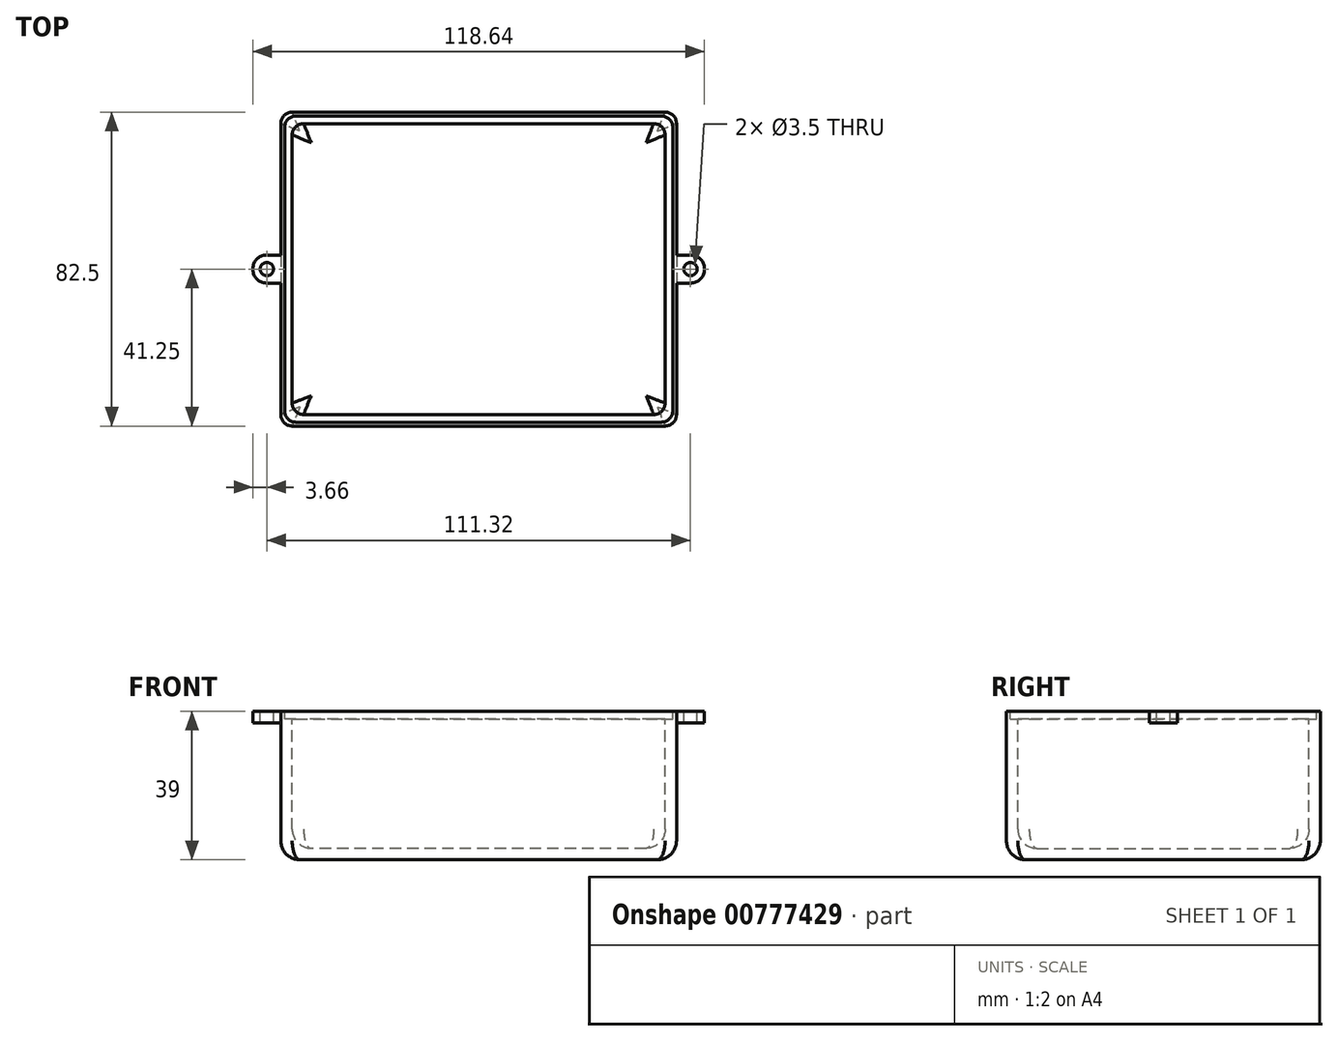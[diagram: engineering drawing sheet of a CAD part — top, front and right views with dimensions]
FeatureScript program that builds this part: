
annotation { "Feature Type Name" : "Feature", "Feature Type Description" : "" }
export const myFeature = defineFeature(function(context is Context, id is Id, definition is map)
    precondition{}
    {
        {
            var Q0;
            Q0=qCreatedBy(makeId("Top.planeOp"),FACE);
            var sketch = newSketch(context, id + "F0", { "sketchPlane" : qUnion([Q0])});
            skLineSegment(sketch, "E0.bottom", {"start": v(-52, 41.25) * mm, "end": v(52, 41.25) * mm});
            skLineSegment(sketch, "E0.top", {"start": v(-52, -41.25) * mm, "end": v(52, -41.25) * mm});
            skLineSegment(sketch, "E0.left", {"start": v(-52, 41.25) * mm, "end": v(-52, -41.25) * mm});
            skLineSegment(sketch, "E0.right", {"start": v(52, 41.25) * mm, "end": v(52, -41.25) * mm});
            skSolve(sketch);
        }
        {
            var Q0;
            Q0=makeQuery(id+"F0.imprint","IMPRINT",FACE,{"disambiguationData":[TD([[makeQuery(id+"F0.imprint","IMPRINT",EDGE,{"derivedFrom":sQuery(id+"F0.wireOp",EDGE,"E0.bottom")}),-1.0]])]});
            extrude(context, id + "F1", {"entities" : qUnion([Q0]), "depth" : 39 * mm, "offsetDistance" : 25 * mm});
        }
        {
            var Q0;
            Q0=makeQuery(id+"F1.opExtrude","CAP_FACE",FACE,{"disambiguationData":[OSD([sQuery(id+"F0.wireOp",EDGE,"E0.bottom"),sQuery(id+"F0.wireOp",EDGE,"E0.top"),sQuery(id+"F0.wireOp",EDGE,"E0.left"),sQuery(id+"F0.wireOp",EDGE,"E0.right")])],"isStart":false});
            var sketch = newSketch(context, id + "F2", { "sketchPlane" : qUnion([Q0])});
            skLineSegment(sketch, "E1.bottom", {"start": v(-49, 38.25) * mm, "end": v(49, 38.25) * mm});
            skLineSegment(sketch, "E1.top", {"start": v(-49, -38.25) * mm, "end": v(49, -38.25) * mm});
            skLineSegment(sketch, "E1.left", {"start": v(-49, 38.25) * mm, "end": v(-49, -38.25) * mm});
            skLineSegment(sketch, "E1.right", {"start": v(49, 38.25) * mm, "end": v(49, -38.25) * mm});
            skSolve(sketch);
        }
        {
            var Q0;
            Q0=makeQuery(id+"F2.imprint","IMPRINT",FACE,{"disambiguationData":[TD([[makeQuery(id+"F2.imprint","IMPRINT",EDGE,{"derivedFrom":sQuery(id+"F2.wireOp",EDGE,"E1.bottom")}),-1.0]])]});
            var Q1;
            Q1=makeQuery(id+"F1.opExtrude","CAP_FACE",FACE,{"disambiguationData":[OSD([sQuery(id+"F0.wireOp",EDGE,"E0.bottom"),sQuery(id+"F0.wireOp",EDGE,"E0.top"),sQuery(id+"F0.wireOp",EDGE,"E0.left"),sQuery(id+"F0.wireOp",EDGE,"E0.right")])],"isStart":true});
            extrude(context, id + "F3", {"entities" : qUnion([Q0]), "operationType" : NewBodyOperationType.REMOVE, "endBound" : BoundingType.UP_TO_SURFACE, "oppositeDirection" : true, "depth" : 25 * mm, "endBoundEntityFace" : qUnion([Q1]), "hasOffset" : true, "offsetDistance" : 3 * mm});
        }
        {
            var Q0;
            Q0=makeQuery(id+"F1.opExtrude","CAP_FACE",FACE,{"disambiguationData":[OSD([sQuery(id+"F0.wireOp",EDGE,"E0.bottom"),sQuery(id+"F0.wireOp",EDGE,"E0.top"),sQuery(id+"F0.wireOp",EDGE,"E0.left"),sQuery(id+"F0.wireOp",EDGE,"E0.right")])],"isStart":false});
            var sketch = newSketch(context, id + "F4", { "sketchPlane" : qUnion([Q0])});
            skLineSegment(sketch, "E2.bottom", {"start": v(-51, 40.25) * mm, "end": v(51, 40.25) * mm});
            skLineSegment(sketch, "E2.top", {"start": v(-51, -40.25) * mm, "end": v(51, -40.25) * mm});
            skLineSegment(sketch, "E2.left", {"start": v(-51, 40.25) * mm, "end": v(-51, -40.25) * mm});
            skLineSegment(sketch, "E2.right", {"start": v(51, 40.25) * mm, "end": v(51, -40.25) * mm});
            skSolve(sketch);
        }
        {
            var Q0;
            Q0 = qSketchRegion(id + "F4", true);
            extrude(context, id + "F5", {"entities" : qUnion([Q0]), "operationType" : NewBodyOperationType.REMOVE, "oppositeDirection" : true, "depth" : 2 * mm, "offsetDistance" : 25 * mm});
        }
        {
            var Q0;
            Q0=makeQuery(id+"F1.opExtrude","SWEPT_EDGE",EDGE,{"disambiguationData":[OSD([sQuery(id+"F0.wireOp",EDGE,"E0.top"),sQuery(id+"F0.wireOp",EDGE,"E0.left")])]});
            var Q1;
            Q1=makeQuery(id+"F1.opExtrude","SWEPT_EDGE",EDGE,{"disambiguationData":[OSD([sQuery(id+"F0.wireOp",EDGE,"E0.top"),sQuery(id+"F0.wireOp",EDGE,"E0.right")])]});
            var Q2;
            Q2=makeQuery(id+"F1.opExtrude","SWEPT_EDGE",EDGE,{"disambiguationData":[OSD([sQuery(id+"F0.wireOp",EDGE,"E0.bottom"),sQuery(id+"F0.wireOp",EDGE,"E0.right")])]});
            var Q3;
            Q3=makeQuery(id+"F1.opExtrude","SWEPT_EDGE",EDGE,{"disambiguationData":[OSD([sQuery(id+"F0.wireOp",EDGE,"E0.bottom"),sQuery(id+"F0.wireOp",EDGE,"E0.left")])]});
            var Q4;
            Q4=makeQuery(id+"F5.boolean.opBoolean","COPY",EDGE,{"derivedFrom":makeQuery(id+"F5.opExtrude","SWEPT_EDGE",EDGE,{"disambiguationData":[OSD([sQuery(id+"F4.wireOp",EDGE,"E2.top"),sQuery(id+"F4.wireOp",EDGE,"E2.left")])]})});
            var Q5;
            Q5=makeQuery(id+"F3.boolean.opBoolean","COPY",EDGE,{"derivedFrom":makeQuery(id+"F3.opExtrude","SWEPT_EDGE",EDGE,{"disambiguationData":[OSD([sQuery(id+"F2.wireOp",EDGE,"E1.top"),sQuery(id+"F2.wireOp",EDGE,"E1.left")])]})});
            var Q6;
            Q6=makeQuery(id+"F5.boolean.opBoolean","COPY",EDGE,{"derivedFrom":makeQuery(id+"F5.opExtrude","SWEPT_EDGE",EDGE,{"disambiguationData":[OSD([sQuery(id+"F4.wireOp",EDGE,"E2.bottom"),sQuery(id+"F4.wireOp",EDGE,"E2.left")])]})});
            var Q7;
            Q7=makeQuery(id+"F3.boolean.opBoolean","COPY",EDGE,{"derivedFrom":makeQuery(id+"F3.opExtrude","SWEPT_EDGE",EDGE,{"disambiguationData":[OSD([sQuery(id+"F2.wireOp",EDGE,"E1.bottom"),sQuery(id+"F2.wireOp",EDGE,"E1.left")])]})});
            var Q8;
            Q8=makeQuery(id+"F3.boolean.opBoolean","COPY",EDGE,{"derivedFrom":makeQuery(id+"F3.opExtrude","SWEPT_EDGE",EDGE,{"disambiguationData":[OSD([sQuery(id+"F2.wireOp",EDGE,"E1.bottom"),sQuery(id+"F2.wireOp",EDGE,"E1.right")])]})});
            var Q9;
            Q9=makeQuery(id+"F5.boolean.opBoolean","COPY",EDGE,{"derivedFrom":makeQuery(id+"F5.opExtrude","SWEPT_EDGE",EDGE,{"disambiguationData":[OSD([sQuery(id+"F4.wireOp",EDGE,"E2.bottom"),sQuery(id+"F4.wireOp",EDGE,"E2.right")])]})});
            var Q10;
            Q10=makeQuery(id+"F3.boolean.opBoolean","COPY",EDGE,{"derivedFrom":makeQuery(id+"F3.opExtrude","SWEPT_EDGE",EDGE,{"disambiguationData":[OSD([sQuery(id+"F2.wireOp",EDGE,"E1.top"),sQuery(id+"F2.wireOp",EDGE,"E1.right")])]})});
            var Q11;
            Q11=makeQuery(id+"F5.boolean.opBoolean","COPY",EDGE,{"derivedFrom":makeQuery(id+"F5.opExtrude","SWEPT_EDGE",EDGE,{"disambiguationData":[OSD([sQuery(id+"F4.wireOp",EDGE,"E2.top"),sQuery(id+"F4.wireOp",EDGE,"E2.right")])]})});
            fillet(context, id + "F6", {"entities" : qUnion([Q0, Q1, Q2, Q3, Q4, Q5, Q6, Q7, Q8, Q9, Q10, Q11]), "radius" : 3 * mm, "tangentPropagation" : true, "allowEdgeOverflow" : false});
        }
        {
            var Q0;
            Q0=makeQuery(id+"F1.opExtrude","CAP_EDGE",EDGE,{"disambiguationData":[OSD([sQuery(id+"F0.wireOp",EDGE,"E0.left")])],"isStart":true});
            var Q1;
            {var subQ0=sQuery(id+"F0.wireOp",EDGE,"E0.left");var subQ1=sQuery(id+"F0.wireOp",EDGE,"E0.top");Q1=makeQuery(id+"F6.opFillet","BLEND_EDGE",EDGE,{"blendedFrom":[makeQuery(id+"F1.opExtrude","SWEPT_EDGE",EDGE,{"disambiguationData":[OSD([subQ1,subQ0])]}),makeQuery(id+"F1.opExtrude","CAP_FACE",FACE,{"disambiguationData":[OSD([sQuery(id+"F0.wireOp",EDGE,"E0.bottom"),subQ1,subQ0,sQuery(id+"F0.wireOp",EDGE,"E0.right")])],"isStart":true})],"blendedInto":[makeQuery(id+"F1.opExtrude","CAP_FACE",FACE,{"disambiguationData":[OSD([sQuery(id+"F0.wireOp",EDGE,"E0.bottom"),subQ1,subQ0,sQuery(id+"F0.wireOp",EDGE,"E0.right")])],"isStart":true})]});}
            var Q2;
            Q2=makeQuery(id+"F1.opExtrude","CAP_EDGE",EDGE,{"disambiguationData":[OSD([sQuery(id+"F0.wireOp",EDGE,"E0.top")])],"isStart":true});
            var Q3;
            {var subQ0=sQuery(id+"F0.wireOp",EDGE,"E0.left");var subQ1=sQuery(id+"F0.wireOp",EDGE,"E0.bottom");Q3=makeQuery(id+"F6.opFillet","BLEND_EDGE",EDGE,{"blendedFrom":[makeQuery(id+"F1.opExtrude","SWEPT_EDGE",EDGE,{"disambiguationData":[OSD([subQ1,subQ0])]}),makeQuery(id+"F1.opExtrude","CAP_FACE",FACE,{"disambiguationData":[OSD([subQ1,sQuery(id+"F0.wireOp",EDGE,"E0.top"),subQ0,sQuery(id+"F0.wireOp",EDGE,"E0.right")])],"isStart":true})],"blendedInto":[makeQuery(id+"F1.opExtrude","CAP_FACE",FACE,{"disambiguationData":[OSD([subQ1,sQuery(id+"F0.wireOp",EDGE,"E0.top"),subQ0,sQuery(id+"F0.wireOp",EDGE,"E0.right")])],"isStart":true})]});}
            var Q4;
            Q4=makeQuery(id+"F1.opExtrude","CAP_EDGE",EDGE,{"disambiguationData":[OSD([sQuery(id+"F0.wireOp",EDGE,"E0.bottom")])],"isStart":true});
            var Q5;
            {var subQ0=sQuery(id+"F0.wireOp",EDGE,"E0.right");var subQ1=sQuery(id+"F0.wireOp",EDGE,"E0.bottom");Q5=makeQuery(id+"F6.opFillet","BLEND_EDGE",EDGE,{"blendedFrom":[makeQuery(id+"F1.opExtrude","SWEPT_EDGE",EDGE,{"disambiguationData":[OSD([subQ1,subQ0])]}),makeQuery(id+"F1.opExtrude","CAP_FACE",FACE,{"disambiguationData":[OSD([subQ1,sQuery(id+"F0.wireOp",EDGE,"E0.top"),sQuery(id+"F0.wireOp",EDGE,"E0.left"),subQ0])],"isStart":true})],"blendedInto":[makeQuery(id+"F1.opExtrude","CAP_FACE",FACE,{"disambiguationData":[OSD([subQ1,sQuery(id+"F0.wireOp",EDGE,"E0.top"),sQuery(id+"F0.wireOp",EDGE,"E0.left"),subQ0])],"isStart":true})]});}
            var Q6;
            Q6=makeQuery(id+"F1.opExtrude","CAP_EDGE",EDGE,{"disambiguationData":[OSD([sQuery(id+"F0.wireOp",EDGE,"E0.right")])],"isStart":true});
            var Q7;
            {var subQ0=sQuery(id+"F0.wireOp",EDGE,"E0.right");var subQ1=sQuery(id+"F0.wireOp",EDGE,"E0.top");Q7=makeQuery(id+"F6.opFillet","BLEND_EDGE",EDGE,{"blendedFrom":[makeQuery(id+"F1.opExtrude","SWEPT_EDGE",EDGE,{"disambiguationData":[OSD([subQ1,subQ0])]}),makeQuery(id+"F1.opExtrude","CAP_FACE",FACE,{"disambiguationData":[OSD([sQuery(id+"F0.wireOp",EDGE,"E0.bottom"),subQ1,sQuery(id+"F0.wireOp",EDGE,"E0.left"),subQ0])],"isStart":true})],"blendedInto":[makeQuery(id+"F1.opExtrude","CAP_FACE",FACE,{"disambiguationData":[OSD([sQuery(id+"F0.wireOp",EDGE,"E0.bottom"),subQ1,sQuery(id+"F0.wireOp",EDGE,"E0.left"),subQ0])],"isStart":true})]});}
            var Q8;
            Q8=makeQuery(id+"F3.boolean.opBoolean","COPY",EDGE,{"derivedFrom":makeQuery(id+"F3.opExtrude","CAP_EDGE",EDGE,{"disambiguationData":[OSD([sQuery(id+"F2.wireOp",EDGE,"E1.left")])],"isStart":false})});
            var Q9;
            {var subQ0=sQuery(id+"F2.wireOp",EDGE,"E1.left");var subQ1=sQuery(id+"F2.wireOp",EDGE,"E1.top");Q9=makeQuery(id+"F6.opFillet","BLEND_EDGE",EDGE,{"blendedFrom":[makeQuery(id+"F3.boolean.opBoolean","COPY",EDGE,{"derivedFrom":makeQuery(id+"F3.opExtrude","SWEPT_EDGE",EDGE,{"disambiguationData":[OSD([subQ1,subQ0])]})}),makeQuery(id+"F3.boolean.opBoolean","COPY",FACE,{"derivedFrom":makeQuery(id+"F3.opExtrude","CAP_FACE",FACE,{"disambiguationData":[OSD([sQuery(id+"F2.wireOp",EDGE,"E1.bottom"),subQ1,subQ0,sQuery(id+"F2.wireOp",EDGE,"E1.right")])],"isStart":false})})],"blendedInto":[makeQuery(id+"F3.boolean.opBoolean","COPY",FACE,{"derivedFrom":makeQuery(id+"F3.opExtrude","CAP_FACE",FACE,{"disambiguationData":[OSD([sQuery(id+"F2.wireOp",EDGE,"E1.bottom"),subQ1,subQ0,sQuery(id+"F2.wireOp",EDGE,"E1.right")])],"isStart":false})})]});}
            var Q10;
            Q10=makeQuery(id+"F3.boolean.opBoolean","COPY",EDGE,{"derivedFrom":makeQuery(id+"F3.opExtrude","CAP_EDGE",EDGE,{"disambiguationData":[OSD([sQuery(id+"F2.wireOp",EDGE,"E1.top")])],"isStart":false})});
            var Q11;
            Q11=makeQuery(id+"F3.boolean.opBoolean","COPY",EDGE,{"derivedFrom":makeQuery(id+"F3.opExtrude","CAP_EDGE",EDGE,{"disambiguationData":[OSD([sQuery(id+"F2.wireOp",EDGE,"E1.right")])],"isStart":false})});
            var Q12;
            {var subQ0=sQuery(id+"F2.wireOp",EDGE,"E1.right");var subQ1=sQuery(id+"F2.wireOp",EDGE,"E1.top");Q12=makeQuery(id+"F6.opFillet","BLEND_EDGE",EDGE,{"blendedFrom":[makeQuery(id+"F3.boolean.opBoolean","COPY",EDGE,{"derivedFrom":makeQuery(id+"F3.opExtrude","SWEPT_EDGE",EDGE,{"disambiguationData":[OSD([subQ1,subQ0])]})}),makeQuery(id+"F3.boolean.opBoolean","COPY",FACE,{"derivedFrom":makeQuery(id+"F3.opExtrude","CAP_FACE",FACE,{"disambiguationData":[OSD([sQuery(id+"F2.wireOp",EDGE,"E1.bottom"),subQ1,sQuery(id+"F2.wireOp",EDGE,"E1.left"),subQ0])],"isStart":false})})],"blendedInto":[makeQuery(id+"F3.boolean.opBoolean","COPY",FACE,{"derivedFrom":makeQuery(id+"F3.opExtrude","CAP_FACE",FACE,{"disambiguationData":[OSD([sQuery(id+"F2.wireOp",EDGE,"E1.bottom"),subQ1,sQuery(id+"F2.wireOp",EDGE,"E1.left"),subQ0])],"isStart":false})})]});}
            var Q13;
            {var subQ0=sQuery(id+"F2.wireOp",EDGE,"E1.right");var subQ1=sQuery(id+"F2.wireOp",EDGE,"E1.bottom");Q13=makeQuery(id+"F6.opFillet","BLEND_EDGE",EDGE,{"blendedFrom":[makeQuery(id+"F3.boolean.opBoolean","COPY",EDGE,{"derivedFrom":makeQuery(id+"F3.opExtrude","SWEPT_EDGE",EDGE,{"disambiguationData":[OSD([subQ1,subQ0])]})}),makeQuery(id+"F3.boolean.opBoolean","COPY",FACE,{"derivedFrom":makeQuery(id+"F3.opExtrude","CAP_FACE",FACE,{"disambiguationData":[OSD([subQ1,sQuery(id+"F2.wireOp",EDGE,"E1.top"),sQuery(id+"F2.wireOp",EDGE,"E1.left"),subQ0])],"isStart":false})})],"blendedInto":[makeQuery(id+"F3.boolean.opBoolean","COPY",FACE,{"derivedFrom":makeQuery(id+"F3.opExtrude","CAP_FACE",FACE,{"disambiguationData":[OSD([subQ1,sQuery(id+"F2.wireOp",EDGE,"E1.top"),sQuery(id+"F2.wireOp",EDGE,"E1.left"),subQ0])],"isStart":false})})]});}
            var Q14;
            Q14=makeQuery(id+"F3.boolean.opBoolean","COPY",EDGE,{"derivedFrom":makeQuery(id+"F3.opExtrude","CAP_EDGE",EDGE,{"disambiguationData":[OSD([sQuery(id+"F2.wireOp",EDGE,"E1.bottom")])],"isStart":false})});
            var Q15;
            {var subQ0=sQuery(id+"F2.wireOp",EDGE,"E1.left");var subQ1=sQuery(id+"F2.wireOp",EDGE,"E1.bottom");Q15=makeQuery(id+"F6.opFillet","BLEND_EDGE",EDGE,{"blendedFrom":[makeQuery(id+"F3.boolean.opBoolean","COPY",EDGE,{"derivedFrom":makeQuery(id+"F3.opExtrude","SWEPT_EDGE",EDGE,{"disambiguationData":[OSD([subQ1,subQ0])]})}),makeQuery(id+"F3.boolean.opBoolean","COPY",FACE,{"derivedFrom":makeQuery(id+"F3.opExtrude","CAP_FACE",FACE,{"disambiguationData":[OSD([subQ1,sQuery(id+"F2.wireOp",EDGE,"E1.top"),subQ0,sQuery(id+"F2.wireOp",EDGE,"E1.right")])],"isStart":false})})],"blendedInto":[makeQuery(id+"F3.boolean.opBoolean","COPY",FACE,{"derivedFrom":makeQuery(id+"F3.opExtrude","CAP_FACE",FACE,{"disambiguationData":[OSD([subQ1,sQuery(id+"F2.wireOp",EDGE,"E1.top"),subQ0,sQuery(id+"F2.wireOp",EDGE,"E1.right")])],"isStart":false})})]});}
            fillet(context, id + "F7", {"entities" : qUnion([Q0, Q1, Q2, Q3, Q4, Q5, Q6, Q7, Q8, Q9, Q10, Q11, Q12, Q13, Q14, Q15]), "radius" : 5 * mm, "tangentPropagation" : true, "allowEdgeOverflow" : false});
        }
        {
            var Q0;
            Q0=makeQuery(id+"F1.opExtrude","CAP_FACE",FACE,{"disambiguationData":[OSD([sQuery(id+"F0.wireOp",EDGE,"E0.bottom"),sQuery(id+"F0.wireOp",EDGE,"E0.top"),sQuery(id+"F0.wireOp",EDGE,"E0.left"),sQuery(id+"F0.wireOp",EDGE,"E0.right")])],"isStart":false});
            var sketch = newSketch(context, id + "F8", { "sketchPlane" : qUnion([Q0])});
            skLineSegment(sketch, "E3.bottom", {"start": v(52, -3.66) * mm, "end": v(59.32, -3.66) * mm});
            skLineSegment(sketch, "E3.top", {"start": v(52, 3.66) * mm, "end": v(59.32, 3.66) * mm});
            skLineSegment(sketch, "E3.left", {"start": v(52, -3.66) * mm, "end": v(52, 3.66) * mm});
            skLineSegment(sketch, "E3.right", {"start": v(59.32, -3.66) * mm, "end": v(59.32, 3.66) * mm});
            skLineSegment(sketch, "E4.bottom", {"start": v(-52, 3.66) * mm, "end": v(-59.32, 3.66) * mm});
            skLineSegment(sketch, "E4.top", {"start": v(-52, -3.66) * mm, "end": v(-59.32, -3.66) * mm});
            skLineSegment(sketch, "E4.left", {"start": v(-52, 3.66) * mm, "end": v(-52, -3.66) * mm});
            skLineSegment(sketch, "E4.right", {"start": v(-59.32, 3.66) * mm, "end": v(-59.32, -3.66) * mm});
            skCircle(sketch, "E5", {"center": v(55.66, 0) * mm, "radius": 1.75 * mm});
            skCircle(sketch, "E6", {"center": v(-55.66, 0) * mm, "radius": 1.75 * mm});
            skPoint(sketch, "E6.centerSnap0", {"position": v(51, 0) * mm});
            skSolve(sketch);
        }
        {
            var Q0;
            Q0 = qSketchRegion(id + "F8", true);
            extrude(context, id + "F9", {"entities" : qUnion([Q0]), "operationType" : NewBodyOperationType.ADD, "oppositeDirection" : true, "depth" : 3 * mm, "offsetDistance" : 25 * mm});
        }
        {
            var Q0;
            Q0=makeQuery(id+"F9.opExtrude","SWEPT_EDGE",EDGE,{"disambiguationData":[OSD([sQuery(id+"F0.wireOp",EDGE,"E0.left"),sQuery(id+"F8.wireOp",EDGE,"E4.top"),sQuery(id+"F8.wireOp",EDGE,"E4.left")])]});
            var Q1;
            Q1=makeQuery(id+"F9.opExtrude","SWEPT_EDGE",EDGE,{"disambiguationData":[OSD([sQuery(id+"F8.wireOp",EDGE,"E4.top"),sQuery(id+"F8.wireOp",EDGE,"E4.right")])]});
            var Q2;
            Q2=makeQuery(id+"F9.opExtrude","SWEPT_EDGE",EDGE,{"disambiguationData":[OSD([sQuery(id+"F8.wireOp",EDGE,"E4.bottom"),sQuery(id+"F8.wireOp",EDGE,"E4.right")])]});
            var Q3;
            Q3=makeQuery(id+"F9.opExtrude","SWEPT_EDGE",EDGE,{"disambiguationData":[OSD([sQuery(id+"F0.wireOp",EDGE,"E0.left"),sQuery(id+"F8.wireOp",EDGE,"E4.bottom"),sQuery(id+"F8.wireOp",EDGE,"E4.left")])]});
            var Q4;
            Q4=makeQuery(id+"F9.opExtrude","SWEPT_EDGE",EDGE,{"disambiguationData":[OSD([sQuery(id+"F0.wireOp",EDGE,"E0.right"),sQuery(id+"F8.wireOp",EDGE,"E3.bottom"),sQuery(id+"F8.wireOp",EDGE,"E3.left")])]});
            var Q5;
            Q5=makeQuery(id+"F9.opExtrude","SWEPT_EDGE",EDGE,{"disambiguationData":[OSD([sQuery(id+"F8.wireOp",EDGE,"E3.bottom"),sQuery(id+"F8.wireOp",EDGE,"E3.right")])]});
            var Q6;
            Q6=makeQuery(id+"F9.opExtrude","SWEPT_EDGE",EDGE,{"disambiguationData":[OSD([sQuery(id+"F8.wireOp",EDGE,"E3.top"),sQuery(id+"F8.wireOp",EDGE,"E3.right")])]});
            var Q7;
            Q7=makeQuery(id+"F9.opExtrude","SWEPT_EDGE",EDGE,{"disambiguationData":[OSD([sQuery(id+"F0.wireOp",EDGE,"E0.right"),sQuery(id+"F8.wireOp",EDGE,"E3.top"),sQuery(id+"F8.wireOp",EDGE,"E3.left")])]});
            fillet(context, id + "F10", {"entities" : qUnion([Q0, Q1, Q2, Q3, Q4, Q5, Q6, Q7]), "radius" : 3.5 * mm, "tangentPropagation" : true, "allowEdgeOverflow" : false});
        }
    });
